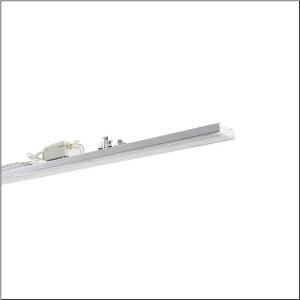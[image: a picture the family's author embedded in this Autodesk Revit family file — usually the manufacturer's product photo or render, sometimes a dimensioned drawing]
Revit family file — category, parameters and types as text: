
# Revit family: licross_21_recessed_ho_52tl1edn4dxs
name_source: partatom
category: Lighting Fixtures
units: mm (PartAtom-declared; Revit-internal decimal feet)

## family parameters
Cut with Voids When Loaded = No
Host = Face
Light Source = No
Part Type = Normal
Room Calculation Point = No
Round Connector Dimension = Use Diameter
Shared = No

## types (1)
- --- (1 x LED, 13000 lm, 74.4 W, 4000K)
    Apparent Load = 74 VA
    CIE Flux Codes = 85 95 99 100 100
    Color Rendering = 80
    Color Temperature = 4000K
    Default Elevation = 1800 mm
    Description = Licross 21 Recessed HO, luminaire insert, of sheet steel, galvanised, coil coated, white, length: 1.500mm, width: 66mm, height: 67mm, LED rated luminous flux: 13.000lm, light colour: 840, SDCM (Standard Deviation of Colour Matching)MacAdam ≤ 3 SDCM (initial), control gear: DALI 2, with plug, 5-pole, with phase selection, mains connection: 220..240V, AC, 50/60Hz, rated input power: 74W, internal wiring halogen-free, primary light control with lens, of plastic, primary optical cover: cover, of PMMA, light emission: direct distribution, primary light characteristic: symmetric, protection rating (complete): IP40, insulation class (complete): insulation class I (protective earthing), certification: CE, ENEC, VDE, UKCA, protection symbol: D if used in an environment without relevant dust loads with corresponding accessories, impact resistance: IK06, permissible ambient temperature for indoor applications: -25..+30°C, corresponds to IFS (International Featured Standards) requirements for safety and quality in the food industry, reducing of maximum allowable ambient temperature of 5°C with ceiling mounting, LABS conformity tested according to VDMA 24364:2018-05, The light source and the operating device comply with the requirements of the Ecodesign Regulation (EU) 2019/2020 and are replaceable in accordance with this regulation, packaging unit: 1 piece
    Height = 58 mm
    Lamp = 1 x LED
    Lamp Light Flux = 13000 lm
    Lamp Power = 74.4 W
    Lamp count = 1
    Length = 1500 mm
    Luminous efficacy = 175 lm/W
    Manufacturer = Siteco
    ModVariant = No
    Model = 52TL1EDN4DXS
    Mounting Place = Ceiling
    Mounting Type = Pendant
    Number of Poles = 1
    OnlyDefault = Yes
    Power Factor = 1
    Product Name = Licross 21 Recessed HO
    Product group = luminaire insert | ceiling pendant
    ProductGroupID = 901
    Protection Class = Protection class I
    Protection Degree = IP 40
    RLX_Detail_Level = 1
    RLX_Emergency_Light_Flux = 0 lm
    RLX_Emergency_Type = 0
    RLX_Emergency_Type_DB = No
    RlxData = <blob elided: 24969 chars, md5=be3cd179>
    Socket = socket
    Standby Power = 0 W
    System Light Flux = 13000 lm
    System Power = 74 W
    Type Comments = factory setting: luminous flux: 100 % | dim-lin: 254 | 426 mA
    Type Image = l_1296930.jpg
    URL = http://relux.com
    VarID = @adj_126819
    Voltage = 0 V
    Weight = 0.00 kg
    Width = 66 mm

## geometry (parser evidence)
native form markers: Blend x4, Sweep x9
no freeform markers — native parametric forms only
